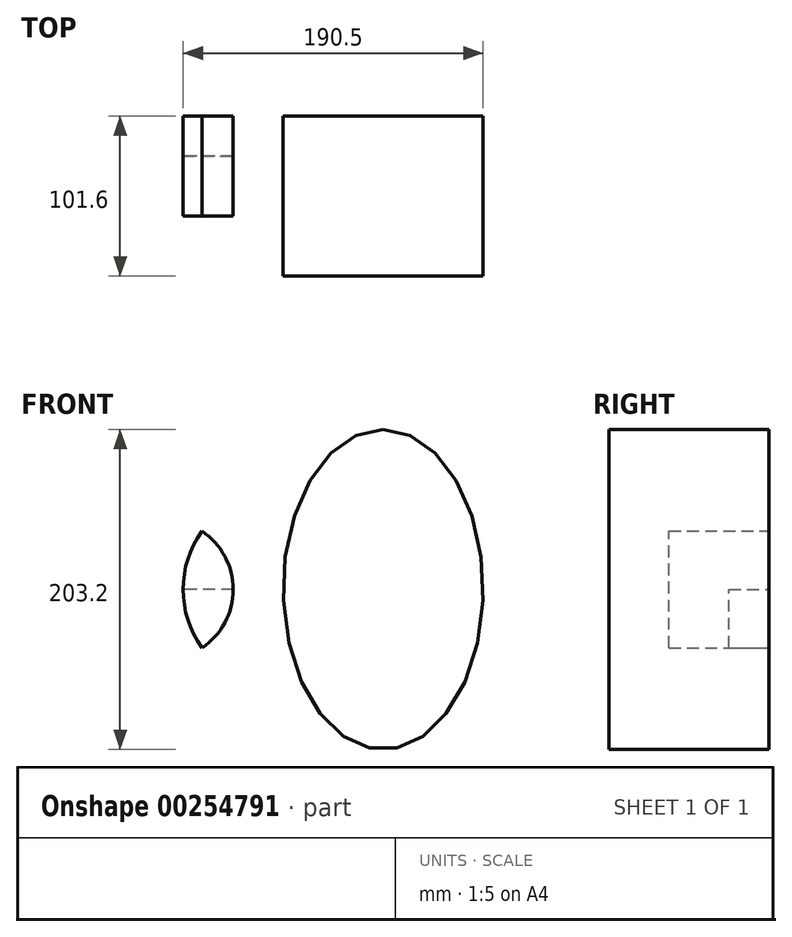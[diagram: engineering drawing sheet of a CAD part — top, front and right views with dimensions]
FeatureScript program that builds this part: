
annotation { "Feature Type Name" : "Feature", "Feature Type Description" : "" }
export const myFeature = defineFeature(function(context is Context, id is Id, definition is map)
    precondition{}
    {
        {
            var Q0;
            Q0=qCreatedBy(makeId("Front.planeOp"),FACE);
            var sketch = newSketch(context, id + "F0", { "sketchPlane" : qUnion([Q0])});
            skLineSegment(sketch, "E0", {"start": v(0, 0) * mm, "end": v(-76.2, 0) * mm});
            skCircle(sketch, "E1", {"center": v(-76.2, 0) * mm, "radius": 44.45 * mm});
            skLineSegment(sketch, "E2", {"start": v(-31.75, 0) * mm, "end": v(-63.5, 0) * mm});
            skCircle(sketch, "E3", {"center": v(0, 0) * mm, "radius": 63.5 * mm});
            skLineSegment(sketch, "E4", {"start": v(63.5, 0) * mm, "end": v(63.5, 101.6) * mm});
            skEllipse(sketch, "E5", {"center": v(63.5, 0) * mm, "majorRadius": 101.6 * mm, "minorRadius": 63.5 * mm, "majorAxis": v(0, 1)});
            skSolve(sketch);
        }
        {
            var Q0;
            {var subQ0=sQuery(id+"F0.wireOp",EDGE,"E3");var subQ1=sQuery(id+"F0.wireOp",EDGE,"E1");var subQ2=makeQuery(id+"F0.imprint","INTERSECT",VERTEX,{"disambiguationData":[OD(0.0)],"derivedFrom":[subQ1,subQ0]});Q0=makeQuery(id+"F0.imprint","IMPRINT",FACE,{"disambiguationData":[TD([[makeQuery(id+"F0.imprint","IMPRINT",EDGE,{"disambiguationData":[TD([[subQ2,-1.0]])],"derivedFrom":subQ1}),1.0]])]});}
            extrude(context, id + "F1", {"entities" : qUnion([Q0]), "depth" : 25.4 * mm});
        }
        {
            var Q0;
            {var subQ3=sQuery(id+"F0.wireOp",EDGE,"E1");var subQ5=sQuery(id+"F0.wireOp",EDGE,"E3");var subQ6=makeQuery(id+"F0.imprint","INTERSECT",VERTEX,{"disambiguationData":[OD(0.0)],"derivedFrom":[subQ3,subQ5]});Q0=makeQuery(id+"F0.imprint","IMPRINT",FACE,{"disambiguationData":[TD([[makeQuery(id+"F0.imprint","IMPRINT",EDGE,{"disambiguationData":[TD([[subQ6,1.0]])],"derivedFrom":subQ5}),1.0]])]});}
            var Q1;
            {var subQ0=sQuery(id+"F0.wireOp",EDGE,"E2");Q1=makeQuery(id+"F0.imprint","IMPRINT",FACE,{"disambiguationData":[TD([[makeQuery(id+"F0.imprint","IMPRINT",EDGE,{"derivedFrom":subQ0}),-1.0]])]});}
            var Q2;
            {var subQ0=sQuery(id+"F0.wireOp",EDGE,"E2");Q2=makeQuery(id+"F0.imprint","IMPRINT",FACE,{"disambiguationData":[TD([[makeQuery(id+"F0.imprint","IMPRINT",EDGE,{"derivedFrom":subQ0}),1.0]])]});}
            var Q3;
            {var subQ3=sQuery(id+"F0.wireOp",EDGE,"E1");var subQ5=sQuery(id+"F0.wireOp",EDGE,"E3");var subQ6=makeQuery(id+"F0.imprint","INTERSECT",VERTEX,{"disambiguationData":[OD(1.0)],"derivedFrom":[subQ3,subQ5]});Q3=makeQuery(id+"F0.imprint","IMPRINT",FACE,{"disambiguationData":[TD([[makeQuery(id+"F0.imprint","IMPRINT",EDGE,{"disambiguationData":[TD([[subQ6,-1.0]])],"derivedFrom":subQ5}),1.0]])]});}
            extrude(context, id + "F2", {"entities" : qUnion([Q0, Q1, Q2, Q3]), "depth" : 63.5 * mm});
        }
        {
            var Q0;
            {var subQ0=sQuery(id+"F0.wireOp",EDGE,"E4");Q0=makeQuery(id+"F0.imprint","IMPRINT",FACE,{"disambiguationData":[TD([[makeQuery(id+"F0.imprint","IMPRINT",EDGE,{"derivedFrom":subQ0}),-1.0]])]});}
            var Q1;
            {var subQ0=sQuery(id+"F0.wireOp",EDGE,"E4");Q1=makeQuery(id+"F0.imprint","IMPRINT",FACE,{"disambiguationData":[TD([[makeQuery(id+"F0.imprint","IMPRINT",EDGE,{"derivedFrom":subQ0}),1.0]])]});}
            var Q2;
            {var subQ0=sQuery(id+"F0.wireOp",EDGE,"E3");var subQ1=makeQuery(id+"F0.imprint","INTERSECT",VERTEX,{"derivedFrom":[subQ0,sQuery(id+"F0.wireOp",EDGE,"E4")]});Q2=makeQuery(id+"F0.imprint","IMPRINT",FACE,{"disambiguationData":[TD([[makeQuery(id+"F0.imprint","IMPRINT",EDGE,{"disambiguationData":[TD([[subQ1,-1.0]])],"derivedFrom":subQ0}),1.0]])]});}
            extrude(context, id + "F3", {"entities" : qUnion([Q0, Q1, Q2]), "depth" : 101.6 * mm});
        }
    });
